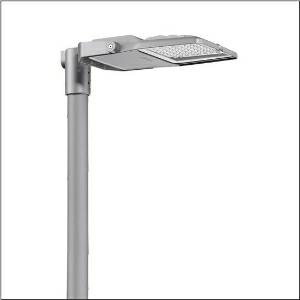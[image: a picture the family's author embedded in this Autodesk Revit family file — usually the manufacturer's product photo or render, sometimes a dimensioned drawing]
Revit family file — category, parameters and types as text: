
# Revit family: floodlight_fl_21_iq_mini___pl52_5xa7772b2d3a_55c6
name_source: partatom
category: Lighting Fixtures
units: mm (PartAtom-declared; Revit-internal decimal feet)

## family parameters
Cut with Voids When Loaded = No
Host = Face
Light Source = No
Part Type = Normal
Room Calculation Point = No
Round Connector Dimension = Use Diameter
Shared = No

## types (1)
- --- (1 x LED, 6240 lm, 45.5 W, 3000K)
    Apparent Load = 46 VA
    CIE Flux Codes = 26 60 98 100 100
    Color Rendering = 70
    Color Temperature = 3000K
    Default Elevation = 1800 mm
    Description = Floodlight FL 21 iQ mini, floodlight, primary light control with lens, of PMMA, primary optical cover: protective disc, of toughened safety glass, transparent, light distribution: PL52, light emission: direct distribution, installation type: surface-mounted, LED, High Power LED, rated luminous flux: 6.240lm, luminous efficacy: 137lm/W, light colour: 730, colour temperature: 3000K, control gear: iQ Street-Remote/DALI, control: Auto-Match, Temp-Guard, Night-Set, Smart-Wire, Desk-Remote (wireless, voltage-free reading and setting of iQ features in the workshop via application-optimized NFC function/RFID function), optimised constant luminous flux control (CLO 2.0), Light-Fading, Lumen-Switch, with terminal, 6-pole, mains connection: 220..240V, AC, 50/60Hz, start of lifetime: 46W, end of service life: 48W, reduction: 22W, luminaire housing, of diecast aluminium, powder-coated, Siteco® metallic grey (DB 702S), corrosivity category C5 mid according to DIN EN ISO 12944, suitable for swimming pools, chlorine-resistant, sealing non-destructively replaceable, please order mast flange separately, mast bracket, of steel, galvanised, powder-coated, protection rating (complete): IP66, insulation class (complete): insulation class II (safety insulation), certification: CE, ENEC, VDE, protection symbol: D, impact resistance: IK08, permissible operating ambient temperature: -40..+40°C, permissible operating ambient temperature for outdoor applications: -40..+50°C, standard: DIN EN 12944, LABS conformity tested according to VDMA 24364:2018-05, packaging unit: 1 piece

Light Distribution: PL52
    Height = 70 mm
    Lamp = 1 x LED
    Lamp Light Flux = 6240 lm
    Lamp Power = 45.5 W
    Lamp count = 1
    Length = 485 mm
    Luminous efficacy = 137 lm/W
    Manufacturer = Siteco
    ModVariant = No
    Model = 5XA7772B2D3A
    Number of Poles = 1
    OnlyDefault = Yes
    Power Factor = 1
    Product Name = Floodlight FL 21 iQ mini | PL52
    Product group = floodlight | pylon annexe
    ProductGroupID = 6200
    Protection Class = Protection class II
    Protection Degree = IP 66
    RLX_Detail_Level = 1
    RLX_Emergency_Light_Flux = 0 lm
    RLX_Emergency_Type = 0
    RLX_Emergency_Type_DB = No
    RlxData = <blob elided: 101405 chars, md5=1d9dac7a>
    Socket = socket
    Standby Power = 0 W
    System Light Flux = 6240 lm
    System Power = 46 W
    Type Comments = factory setting: luminous flux: 100 % | dim-lin: 254 | 463 mA
    Type Image = l_1007125.jpg
    URL = http://relux.com
    VarID = @adj_164844
    Voltage = 0 V
    Weight = 0.00 kg
    Width = 337 mm

## geometry (parser evidence)
native form markers: Blend x4, Sweep x14
no freeform markers — native parametric forms only
